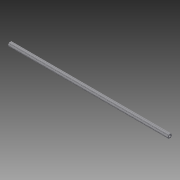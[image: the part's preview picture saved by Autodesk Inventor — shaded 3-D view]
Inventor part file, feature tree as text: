
AUTODESK INVENTOR PART (.ipt)
format: ipt  version: 2015 SP1 (Build 190203100, 203)  size: 150,528 bytes
history: native  units: in
note: dims shown in document units (in); Inventor stores cm internally (conversion verified against a paired STEP export)
features: extrude x1, sketch x1
ambient origin geometry x8: Origin, YZ Plane, XZ Plane, XY Plane, X Axis, Y Axis, Z Axis, Center Point
bodies: Solid1 (feature_tree)
feature tree (2):
  extrude  "Extrusion1"  Depth=0.5in
  sketch  "Sketch1"  dims[d0=0.5in d1=0.5in d2=0.5in d3=120.0deg d4=120.0deg d5=0.25in d6=0.25in d7=0.25in d11=0.0312in d12=0.0938in d13=0.0938in d14=0.0938in d15=0.0938in d16=0.0938in d17=0.0938in d18=0.0938in d19=0.0938in d20=0.0938in d21=0.0938in d22=0.0938in d23=0.0938in d24=150.0deg d25=150.0deg d26=150.0deg d27=90.0deg d28=90.0deg d29=30.0deg d30=30.0deg d31=30.0deg d32=30.0deg d33=90.0deg d34=90.0deg d35=150.0deg d36=0.25in d37=21.5in d38=0.0in]
